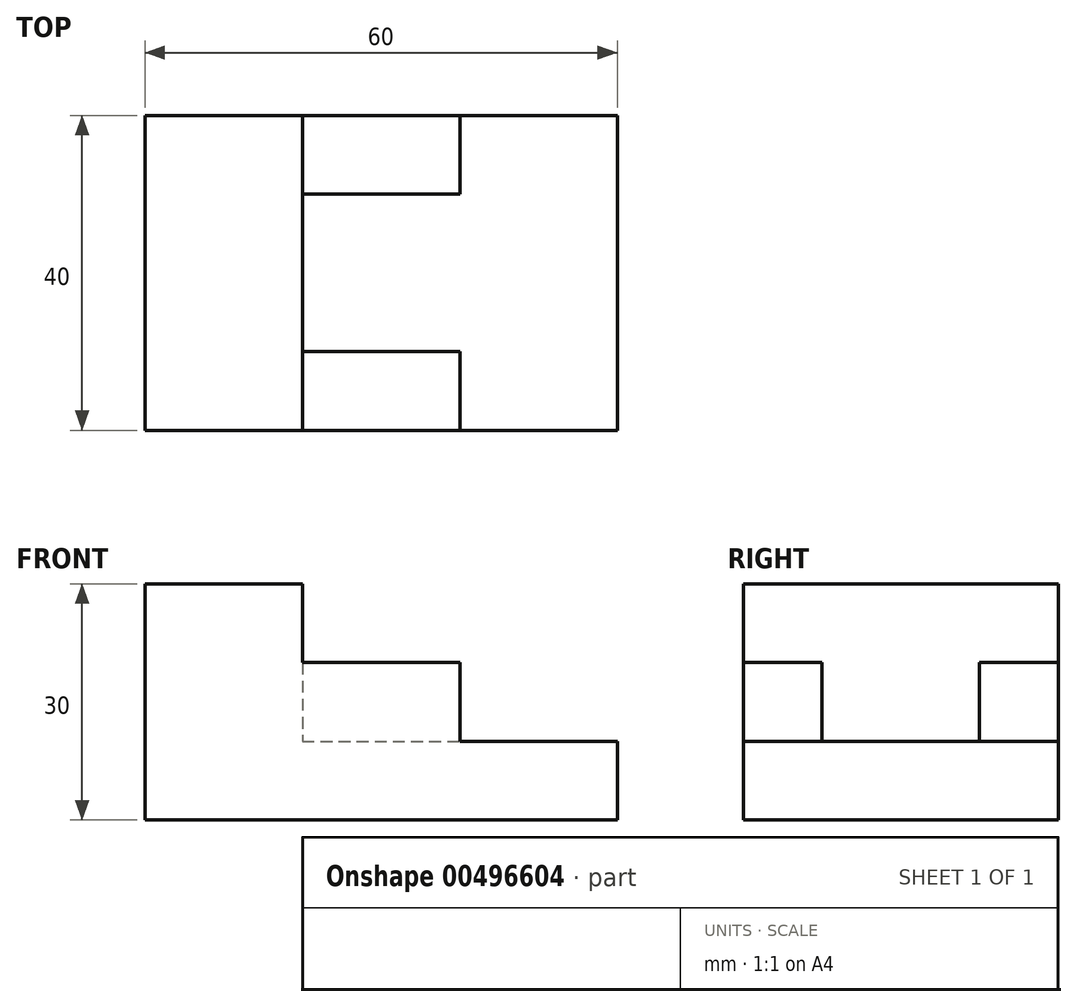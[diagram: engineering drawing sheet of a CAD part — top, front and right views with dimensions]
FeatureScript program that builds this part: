
annotation { "Feature Type Name" : "Feature", "Feature Type Description" : "" }
export const myFeature = defineFeature(function(context is Context, id is Id, definition is map)
    precondition{}
    {
        {
            var Q0;
            Q0=qCreatedBy(makeId("Front.planeOp"),FACE);
            var sketch = newSketch(context, id + "F0", { "sketchPlane" : qUnion([Q0])});
            skLineSegment(sketch, "E0", {"start": v(0, 0) * mm, "end": v(0, 30) * mm});
            skLineSegment(sketch, "E1", {"start": v(0, 0) * mm, "end": v(60, 0) * mm});
            skLineSegment(sketch, "E2", {"start": v(60, 0) * mm, "end": v(60, 10) * mm});
            skLineSegment(sketch, "E3", {"start": v(60, 10) * mm, "end": v(20, 10) * mm});
            skLineSegment(sketch, "E4", {"start": v(20, 10) * mm, "end": v(20, 30) * mm});
            skLineSegment(sketch, "E5", {"start": v(20, 30) * mm, "end": v(0, 30) * mm});
            skSolve(sketch);
        }
        {
            var Q0;
            Q0=makeQuery(id+"F0.imprint","IMPRINT",FACE,{"disambiguationData":[TD([[makeQuery(id+"F0.imprint","IMPRINT",EDGE,{"derivedFrom":sQuery(id+"F0.wireOp",EDGE,"E0")}),-1.0]])]});
            extrude(context, id + "F1", {"entities" : qUnion([Q0]), "oppositeDirection" : true, "depth" : 40 * mm});
        }
        {
            var Q0;
            Q0=makeQuery(id+"F1.opExtrude","SWEPT_FACE",FACE,{"disambiguationData":[OSD([sQuery(id+"F0.wireOp",EDGE,"E3")])]});
            var sketch = newSketch(context, id + "F2", { "sketchPlane" : qUnion([Q0])});
            skLineSegment(sketch, "E6.bottom", {"start": v(20, 0) * mm, "end": v(40, 0) * mm});
            skLineSegment(sketch, "E6.top", {"start": v(20, 10) * mm, "end": v(40, 10) * mm});
            skLineSegment(sketch, "E6.left", {"start": v(20, 0) * mm, "end": v(20, 10) * mm});
            skLineSegment(sketch, "E6.right", {"start": v(40, 0) * mm, "end": v(40, 10) * mm});
            skLineSegment(sketch, "E7.bottom", {"start": v(20, 40) * mm, "end": v(40, 40) * mm});
            skLineSegment(sketch, "E7.top", {"start": v(20, 30) * mm, "end": v(40, 30) * mm});
            skLineSegment(sketch, "E7.left", {"start": v(20, 40) * mm, "end": v(20, 30) * mm});
            skLineSegment(sketch, "E7.right", {"start": v(40, 40) * mm, "end": v(40, 30) * mm});
            skSolve(sketch);
        }
        {
            var Q0;
            Q0=makeQuery(id+"F2.imprint","IMPRINT",FACE,{"disambiguationData":[TD([[makeQuery(id+"F2.imprint","IMPRINT",EDGE,{"derivedFrom":sQuery(id+"F2.wireOp",EDGE,"E7.bottom")}),1.0]])]});
            var Q1;
            Q1=makeQuery(id+"F2.imprint","IMPRINT",FACE,{"disambiguationData":[TD([[makeQuery(id+"F2.imprint","IMPRINT",EDGE,{"derivedFrom":sQuery(id+"F2.wireOp",EDGE,"E6.bottom")}),-1.0]])]});
            extrude(context, id + "F3", {"entities" : qUnion([Q0, Q1]), "operationType" : NewBodyOperationType.ADD, "depth" : 10 * mm});
        }
    });
